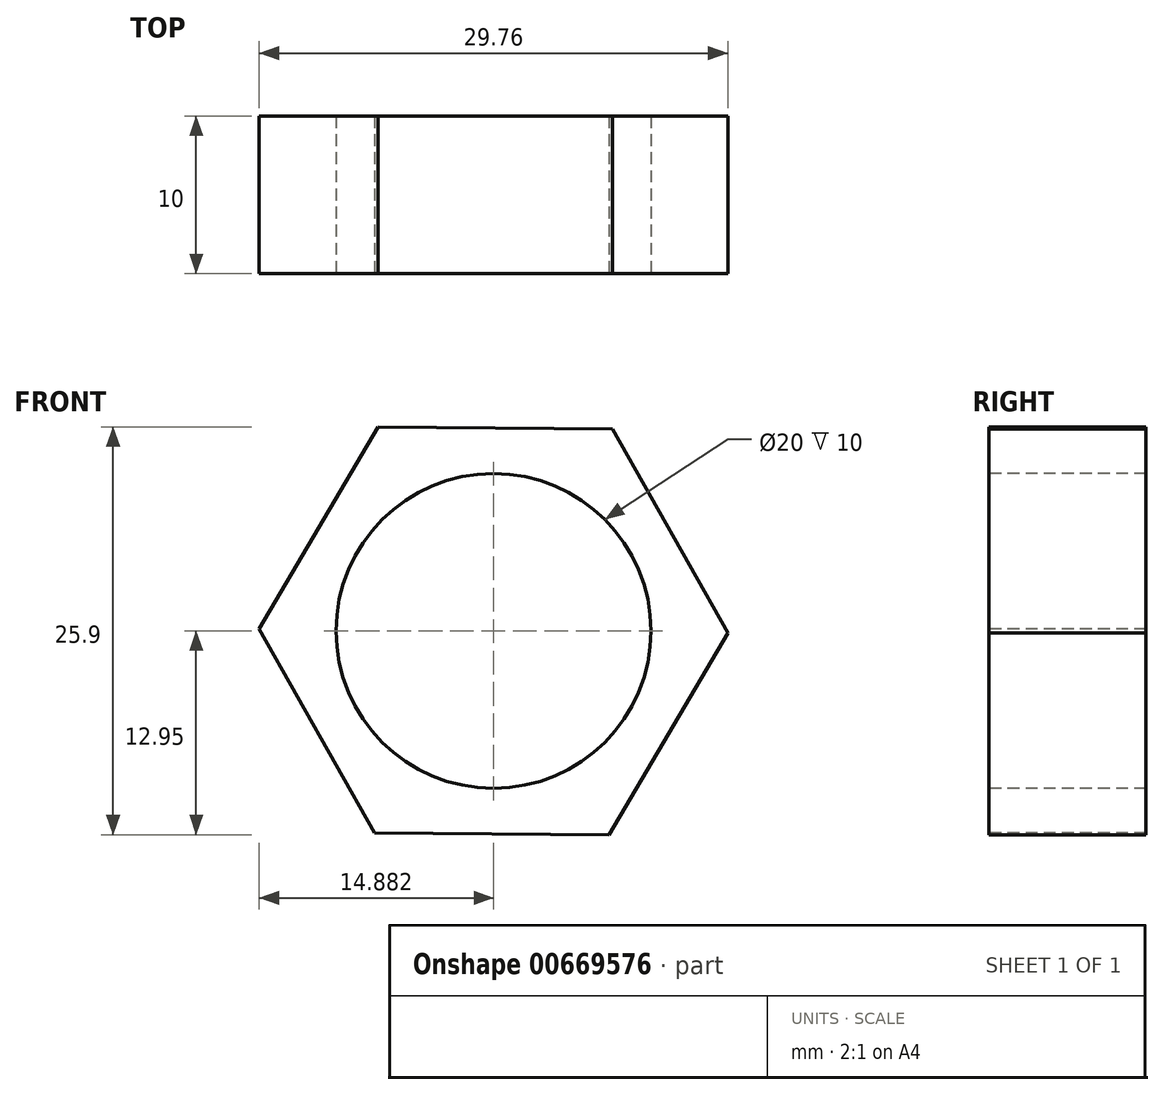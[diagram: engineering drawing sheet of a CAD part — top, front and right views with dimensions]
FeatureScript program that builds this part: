
annotation { "Feature Type Name" : "Feature", "Feature Type Description" : "" }
export const myFeature = defineFeature(function(context is Context, id is Id, definition is map)
    precondition{}
    {
        {
            var Q0;
            Q0=qCreatedBy(makeId("Front.planeOp"),FACE);
            var sketch = newSketch(context, id + "F0", { "sketchPlane" : qUnion([Q0])});
            skCircle(sketch, "E0", {"center": v(-3.37, 0) * mm, "radius": 10 * mm});
            skLineSegment(sketch, "E1.0", {"start": v(3.96, -12.95) * mm, "end": v(-10.91, -12.82) * mm});
            skLineSegment(sketch, "E1.1", {"start": v(-10.91, -12.82) * mm, "end": v(-18.25, 0.12) * mm});
            skLineSegment(sketch, "E1.2", {"start": v(-18.25, 0.12) * mm, "end": v(-10.7, 12.95) * mm});
            skLineSegment(sketch, "E1.3", {"start": v(-10.7, 12.95) * mm, "end": v(4.18, 12.82) * mm});
            skLineSegment(sketch, "E1.4", {"start": v(4.18, 12.82) * mm, "end": v(11.51, -0.12) * mm});
            skLineSegment(sketch, "E1.5", {"start": v(11.51, -0.12) * mm, "end": v(3.96, -12.95) * mm});
            skSolve(sketch);
        }
        {
            var Q0;
            Q0=makeQuery(id+"F0.imprint","IMPRINT",FACE,{"disambiguationData":[TD([[makeQuery(id+"F0.imprint","IMPRINT",EDGE,{"derivedFrom":sQuery(id+"F0.wireOp",EDGE,"E0")}),-1.0]])]});
            extrude(context, id + "F1", {"entities" : qUnion([Q0]), "oppositeDirection" : true, "depth" : 10 * mm, "offsetDistance" : 25 * mm});
        }
    });
